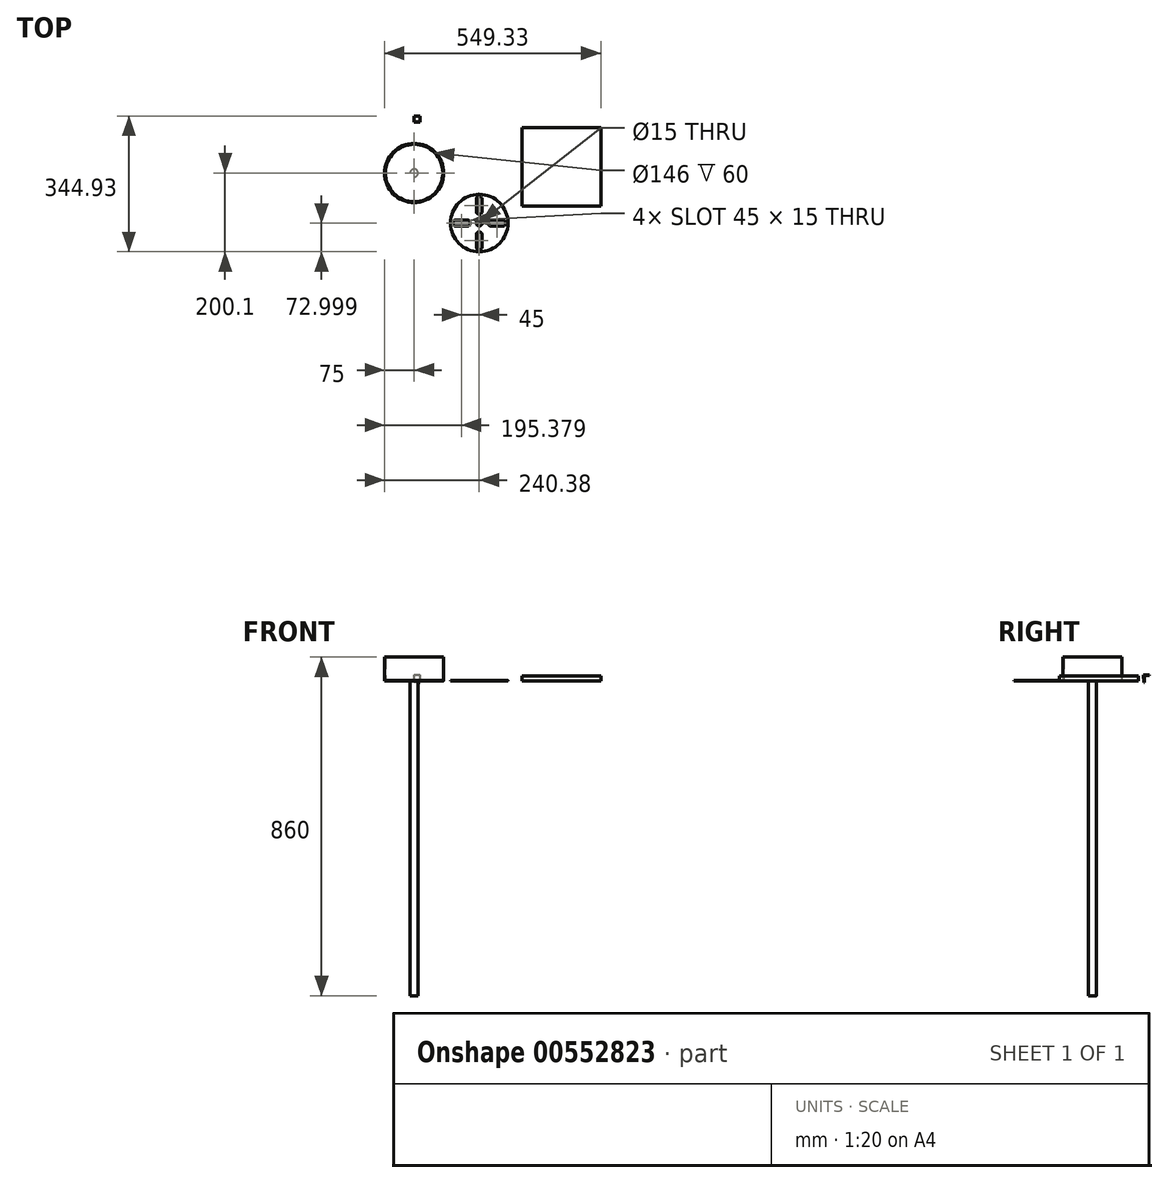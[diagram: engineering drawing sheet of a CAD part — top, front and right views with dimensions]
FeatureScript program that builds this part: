
annotation { "Feature Type Name" : "Feature", "Feature Type Description" : "" }
export const myFeature = defineFeature(function(context is Context, id is Id, definition is map)
    precondition{}
    {
        {
            var Q0;
            Q0=qCreatedBy(makeId("Top.planeOp"),FACE);
            var sketch = newSketch(context, id + "F0", { "sketchPlane" : qUnion([Q0])});
            skCircle(sketch, "E0", {"center": v(0, 0) * mm, "radius": 75 * mm});
            skCircle(sketch, "E1", {"center": v(0, 0) * mm, "radius": 73 * mm});
            skCircle(sketch, "E2", {"center": v(0, 0) * mm, "radius": 10 * mm});
            skLineSegment(sketch, "E3.bottom", {"start": v(274.33, 115.93) * mm, "end": v(474.33, 115.93) * mm});
            skLineSegment(sketch, "E3.top", {"start": v(274.33, -84.07) * mm, "end": v(474.33, -84.07) * mm});
            skLineSegment(sketch, "E3.left", {"start": v(474.33, 115.93) * mm, "end": v(474.33, -84.07) * mm});
            skLineSegment(sketch, "E3.right", {"start": v(274.33, 115.93) * mm, "end": v(274.33, -84.07) * mm});
            skCircle(sketch, "E4", {"center": v(165.38, -127.1) * mm, "radius": 73 * mm});
            skCircle(sketch, "E5", {"center": v(165.38, -127.1) * mm, "radius": 7.5 * mm});
            skArc(sketch, "E6", {"start": v(157.88, -97.1) * mm, "mid": v(165.43, -104.6) * mm, "end": v(172.88, -97) * mm});
            skArc(sketch, "E7", {"start": v(172.88, -67.1) * mm, "mid": v(165.38, -59.6) * mm, "end": v(157.88, -67.1) * mm});
            skLineSegment(sketch, "E8", {"start": v(157.88, -67.1) * mm, "end": v(157.88, -97.1) * mm});
            skLineSegment(sketch, "E9", {"start": v(172.88, -97) * mm, "end": v(172.88, -67.1) * mm});
            skArc(sketch, "E10.1.0", {"start": v(135.38, -134.6) * mm, "mid": v(142.88, -127.05) * mm, "end": v(135.28, -119.6) * mm});
            skLineSegment(sketch, "E10.1.1", {"start": v(135.28, -119.6) * mm, "end": v(105.38, -119.6) * mm});
            skLineSegment(sketch, "E10.1.2", {"start": v(105.38, -134.6) * mm, "end": v(135.38, -134.6) * mm});
            skArc(sketch, "E10.1.3", {"start": v(105.38, -119.6) * mm, "mid": v(97.88, -127.1) * mm, "end": v(105.38, -134.6) * mm});
            skArc(sketch, "E10.2.0", {"start": v(172.88, -157.1) * mm, "mid": v(165.33, -149.6) * mm, "end": v(157.88, -157.2) * mm});
            skLineSegment(sketch, "E10.2.1", {"start": v(157.88, -157.2) * mm, "end": v(157.88, -187.1) * mm});
            skLineSegment(sketch, "E10.2.2", {"start": v(172.88, -187.1) * mm, "end": v(172.88, -157.1) * mm});
            skArc(sketch, "E10.2.3", {"start": v(157.88, -187.1) * mm, "mid": v(165.38, -194.6) * mm, "end": v(172.88, -187.1) * mm});
            skArc(sketch, "E10.3.0", {"start": v(195.38, -119.6) * mm, "mid": v(187.88, -127.15) * mm, "end": v(195.48, -134.6) * mm});
            skLineSegment(sketch, "E10.3.1", {"start": v(195.48, -134.6) * mm, "end": v(225.38, -134.6) * mm});
            skLineSegment(sketch, "E10.3.2", {"start": v(225.38, -119.6) * mm, "end": v(195.38, -119.6) * mm});
            skArc(sketch, "E10.3.3", {"start": v(225.38, -134.6) * mm, "mid": v(232.88, -127.1) * mm, "end": v(225.38, -119.6) * mm});
            skSolve(sketch);
        }
        {
            var Q0;
            Q0=makeQuery(id+"F0.imprint","IMPRINT",FACE,{"disambiguationData":[TD([[makeQuery(id+"F0.imprint","IMPRINT",EDGE,{"derivedFrom":sQuery(id+"F0.wireOp",EDGE,"E0")}),1.0]])]});
            extrude(context, id + "F1", {"entities" : qUnion([Q0]), "depth" : 60 * mm, "offsetDistance" : 25 * mm});
        }
        {
            var Q0;
            Q0=makeQuery(id+"F0.imprint","IMPRINT",FACE,{"disambiguationData":[TD([[makeQuery(id+"F0.imprint","IMPRINT",EDGE,{"derivedFrom":sQuery(id+"F0.wireOp",EDGE,"E2")}),1.0]])]});
            var Q1;
            Q1=sQuery(id+"F0.wireOp",EDGE,"E2");
            extrude(context, id + "F2", {"entities" : qUnion([Q0]), "surfaceEntities" : qUnion([Q1]), "oppositeDirection" : true, "depth" : 800 * mm, "offsetDistance" : 25 * mm});
        }
        {
            var Q0;
            Q0=makeQuery(id+"F0.imprint","IMPRINT",FACE,{"disambiguationData":[TD([[makeQuery(id+"F0.imprint","IMPRINT",EDGE,{"derivedFrom":sQuery(id+"F0.wireOp",EDGE,"E1")}),1.0]])]});
            var Q1;
            Q1=makeQuery(id+"F0.imprint","IMPRINT",FACE,{"disambiguationData":[TD([[makeQuery(id+"F0.imprint","IMPRINT",EDGE,{"derivedFrom":sQuery(id+"F0.wireOp",EDGE,"E0")}),1.0]])]});
            var Q2;
            Q2=makeQuery(id+"F0.imprint","IMPRINT",FACE,{"disambiguationData":[TD([[makeQuery(id+"F0.imprint","IMPRINT",EDGE,{"derivedFrom":sQuery(id+"F0.wireOp",EDGE,"E2")}),1.0]])]});
            extrude(context, id + "F3", {"entities" : qUnion([Q0, Q1, Q2]), "depth" : 1 * mm, "offsetDistance" : 25 * mm});
        }
        {
            var Q0;
            Q0 = qSketchRegion(id + "F0", true);
            var Q1;
            Q1=makeQuery(id+"F0.imprint","IMPRINT",FACE,{"disambiguationData":[TD([[makeQuery(id+"F0.imprint","IMPRINT",EDGE,{"derivedFrom":sQuery(id+"F0.wireOp",EDGE,"E3.bottom")}),-1.0]])]});
            extrude(context, id + "F4", {"entities" : qUnion([Q0, Q1]), "depth" : 12 * mm, "offsetDistance" : 25 * mm});
        }
        {
            var Q0;
            Q0=makeQuery(id+"F4.opExtrude","SWEPT_BODY",BODY,{"disambiguationData":[OSD([sQuery(id+"F0.wireOp",EDGE,"E0"),sQuery(id+"F0.wireOp",EDGE,"E1")])]});
            deleteBodies(context, id + "F5", {"entities" : qUnion([Q0])});
        }
        {
            var Q0;
            Q0=makeQuery(id+"F4.opExtrude","SWEPT_BODY",BODY,{"disambiguationData":[OSD([sQuery(id+"F0.wireOp",EDGE,"E4"),sQuery(id+"F0.wireOp",EDGE,"E5"),sQuery(id+"F0.wireOp",EDGE,"E6"),sQuery(id+"F0.wireOp",EDGE,"E7"),sQuery(id+"F0.wireOp",EDGE,"E8"),sQuery(id+"F0.wireOp",EDGE,"E9"),sQuery(id+"F0.wireOp",EDGE,"E10.1.0"),sQuery(id+"F0.wireOp",EDGE,"E10.1.1"),sQuery(id+"F0.wireOp",EDGE,"E10.1.2"),sQuery(id+"F0.wireOp",EDGE,"E10.1.3"),sQuery(id+"F0.wireOp",EDGE,"E10.2.0"),sQuery(id+"F0.wireOp",EDGE,"E10.2.1"),sQuery(id+"F0.wireOp",EDGE,"E10.2.2"),sQuery(id+"F0.wireOp",EDGE,"E10.2.3"),sQuery(id+"F0.wireOp",EDGE,"E10.3.0"),sQuery(id+"F0.wireOp",EDGE,"E10.3.1"),sQuery(id+"F0.wireOp",EDGE,"E10.3.2"),sQuery(id+"F0.wireOp",EDGE,"E10.3.3")])]});
            deleteBodies(context, id + "F6", {"entities" : qUnion([Q0])});
        }
        {
            var Q0;
            Q0=makeQuery(id+"F0.imprint","IMPRINT",FACE,{"disambiguationData":[TD([[makeQuery(id+"F0.imprint","IMPRINT",EDGE,{"derivedFrom":sQuery(id+"F0.wireOp",EDGE,"E4")}),1.0]])]});
            extrude(context, id + "F7", {"entities" : qUnion([Q0]), "depth" : 1 * mm, "offsetDistance" : 25 * mm});
        }
        {
            var Q0;
            Q0=qCreatedBy(makeId("Right.planeOp"),FACE);
            var sketch = newSketch(context, id + "F8", { "sketchPlane" : qUnion([Q0])});
            skLineSegment(sketch, "E11", {"start": v(144.83, 15.48) * mm, "end": v(129.83, 15.48) * mm});
            skLineSegment(sketch, "E12", {"start": v(129.83, 15.48) * mm, "end": v(129.93, -4.52) * mm});
            skLineSegment(sketch, "E13", {"start": v(129.93, -4.52) * mm, "end": v(131.93, -4.51) * mm});
            skLineSegment(sketch, "E14", {"start": v(131.93, -4.51) * mm, "end": v(131.93, 13.48) * mm});
            skLineSegment(sketch, "E15", {"start": v(131.93, 13.48) * mm, "end": v(144.83, 13.48) * mm});
            skLineSegment(sketch, "E16", {"start": v(144.83, 13.48) * mm, "end": v(144.83, 15.48) * mm});
            skSolve(sketch);
        }
        {
            var Q0;
            Q0=makeQuery(id+"F8.imprint","IMPRINT",FACE,{"disambiguationData":[TD([[makeQuery(id+"F8.imprint","IMPRINT",EDGE,{"derivedFrom":sQuery(id+"F8.wireOp",EDGE,"E11")}),1.0]])]});
            extrude(context, id + "F9", {"entities" : qUnion([Q0]), "depth" : 15 * mm, "offsetDistance" : 25 * mm});
        }
    });
